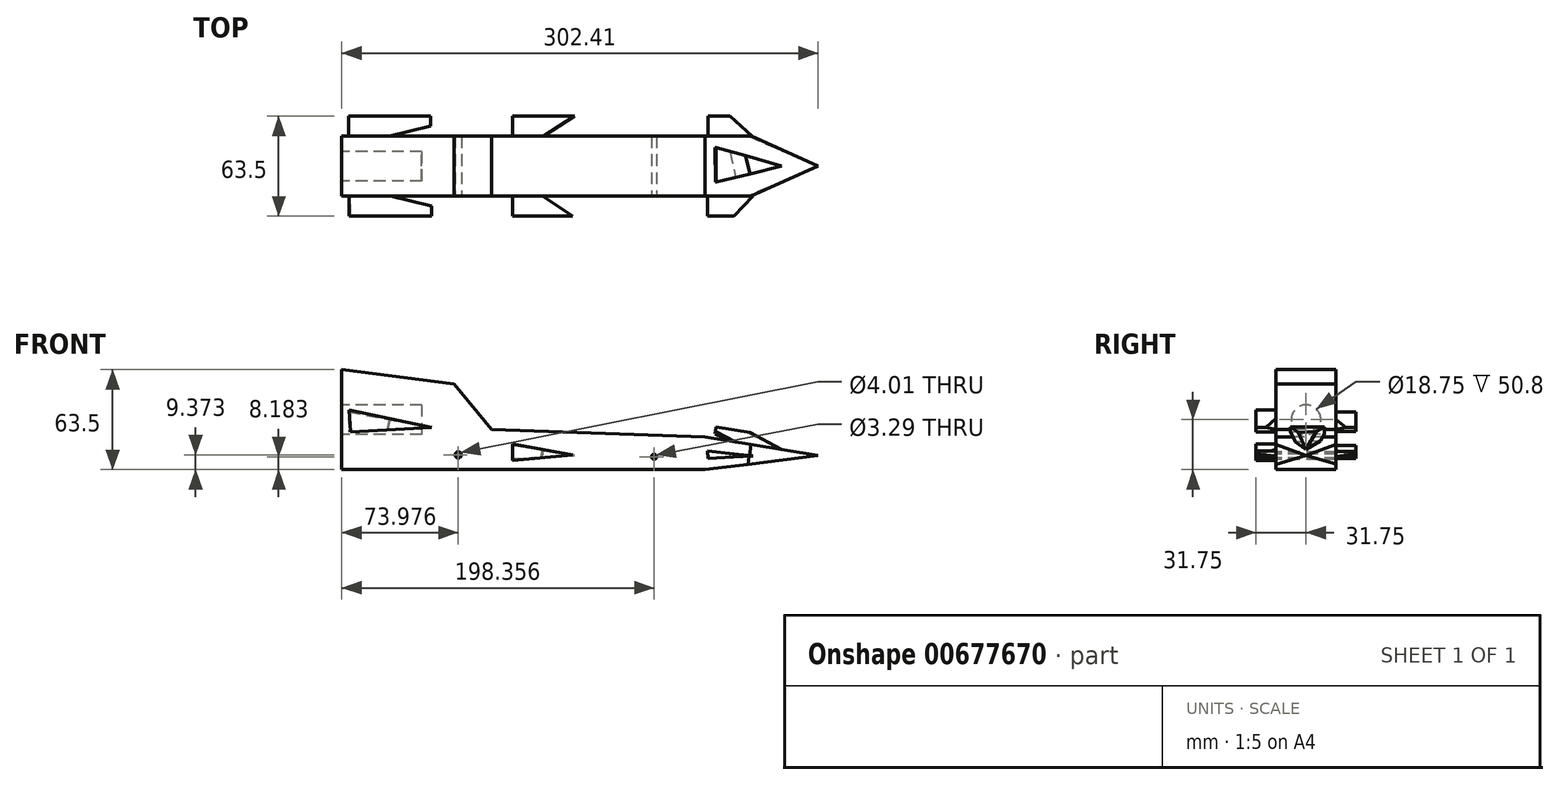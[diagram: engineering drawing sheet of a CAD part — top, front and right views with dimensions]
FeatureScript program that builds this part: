
annotation { "Feature Type Name" : "Feature", "Feature Type Description" : "" }
export const myFeature = defineFeature(function(context is Context, id is Id, definition is map)
    precondition{}
    {
        {
            var Q0;
            Q0=qCreatedBy(makeId("Front.planeOp"),FACE);
            var sketch = newSketch(context, id + "F0", { "sketchPlane" : qUnion([Q0])});
            skLineSegment(sketch, "E0", {"start": v(0, 0) * mm, "end": v(0, 63.5) * mm});
            skLineSegment(sketch, "E1", {"start": v(0, 63.5) * mm, "end": v(302.4, 25.4) * mm});
            skLineSegment(sketch, "E2", {"start": v(302.4, 25.4) * mm, "end": v(302.4, 0) * mm});
            skLineSegment(sketch, "E3", {"start": v(302.4, 0) * mm, "end": v(0, 0) * mm});
            skSolve(sketch);
        }
        {
            var Q0;
            Q0=makeQuery(id+"F0.imprint","IMPRINT",FACE,{"disambiguationData":[TD([[makeQuery(id+"F0.imprint","IMPRINT",EDGE,{"derivedFrom":sQuery(id+"F0.wireOp",EDGE,"E0")}),-1.0]])]});
            extrude(context, id + "F1", {"entities" : qUnion([Q0]), "depth" : 38.1 * mm, "offsetDistance" : 25.4 * mm});
        }
        {
            var Q0;
            Q0=makeQuery(id+"F1.opExtrude","SWEPT_FACE",FACE,{"disambiguationData":[OSD([sQuery(id+"F0.wireOp",EDGE,"E0")])]});
            var sketch = newSketch(context, id + "F2", { "sketchPlane" : qUnion([Q0])});
            skCircle(sketch, "E4", {"center": v(19.05, 31.75) * mm, "radius": 9.38 * mm});
            skPoint(sketch, "E4.centerSnap0", {"position": v(38.1, 31.75) * mm});
            skPoint(sketch, "E4.centerSnap1", {"position": v(19.05, 0) * mm});
            skSolve(sketch);
        }
        {
            var Q0;
            Q0=makeQuery(id+"F1.opExtrude","CAP_FACE",FACE,{"disambiguationData":[OSD([sQuery(id+"F0.wireOp",EDGE,"E0"),sQuery(id+"F0.wireOp",EDGE,"E1"),sQuery(id+"F0.wireOp",EDGE,"E2"),sQuery(id+"F0.wireOp",EDGE,"E3")])],"isStart":false});
            var sketch = newSketch(context, id + "F3", { "sketchPlane" : qUnion([Q0])});
            skLineSegment(sketch, "E5", {"start": v(0, 63.5) * mm, "end": v(71.38, 54.5) * mm});
            skLineSegment(sketch, "E6", {"start": v(71.38, 54.5) * mm, "end": v(95.22, 25.4) * mm});
            skLineSegment(sketch, "E7", {"start": v(95.22, 25.4) * mm, "end": v(302.4, 18.07) * mm});
            skSolve(sketch);
        }
        {
            var Q0;
            {var subQ0=sQuery(id+"F3.wireOp",EDGE,"E6");Q0=makeQuery(id+"F3.imprint","IMPRINT",FACE,{"disambiguationData":[TD([[makeQuery(id+"F3.imprint","IMPRINT",EDGE,{"derivedFrom":subQ0}),1.0]])]});}
            extrude(context, id + "F4", {"entities" : qUnion([Q0]), "operationType" : NewBodyOperationType.REMOVE, "oppositeDirection" : true, "depth" : 38.1 * mm, "offsetDistance" : 25.4 * mm});
        }
        {
            var Q0;
            Q0=makeQuery(id+"F1.opExtrude","CAP_FACE",FACE,{"disambiguationData":[OSD([sQuery(id+"F0.wireOp",EDGE,"E0"),sQuery(id+"F0.wireOp",EDGE,"E1"),sQuery(id+"F0.wireOp",EDGE,"E2"),sQuery(id+"F0.wireOp",EDGE,"E3")])],"isStart":false});
            var sketch = newSketch(context, id + "F5", { "sketchPlane" : qUnion([Q0])});
            skLineSegment(sketch, "E8", {"start": v(302.4, 9.03) * mm, "end": v(230.75, 20.6) * mm});
            skLineSegment(sketch, "E9", {"start": v(302.4, 9.03) * mm, "end": v(232.62, 0) * mm});
            skSolve(sketch);
        }
        {
            var Q0;
            {var subQ0=sQuery(id+"F5.wireOp",EDGE,"E8");Q0=makeQuery(id+"F5.imprint","IMPRINT",FACE,{"disambiguationData":[TD([[makeQuery(id+"F5.imprint","IMPRINT",EDGE,{"derivedFrom":subQ0}),-1.0]])]});}
            extrude(context, id + "F6", {"entities" : qUnion([Q0]), "operationType" : NewBodyOperationType.REMOVE, "oppositeDirection" : true, "depth" : 38.1 * mm, "offsetDistance" : 25.4 * mm});
        }
        {
            var Q0;
            Q0=makeQuery(id+"F1.opExtrude","CAP_FACE",FACE,{"disambiguationData":[OSD([sQuery(id+"F0.wireOp",EDGE,"E0"),sQuery(id+"F0.wireOp",EDGE,"E1"),sQuery(id+"F0.wireOp",EDGE,"E2"),sQuery(id+"F0.wireOp",EDGE,"E3")])],"isStart":false});
            var sketch = newSketch(context, id + "F7", { "sketchPlane" : qUnion([Q0])});
            skLineSegment(sketch, "E10", {"start": v(302.4, 9.03) * mm, "end": v(230.75, 0) * mm});
            skSolve(sketch);
        }
        {
            var Q0;
            {var subQ0=sQuery(id+"F7.wireOp",EDGE,"E10");Q0=makeQuery(id+"F7.imprint","IMPRINT",FACE,{"disambiguationData":[TD([[makeQuery(id+"F7.imprint","IMPRINT",EDGE,{"derivedFrom":subQ0}),1.0]])]});}
            extrude(context, id + "F8", {"entities" : qUnion([Q0]), "operationType" : NewBodyOperationType.REMOVE, "oppositeDirection" : true, "depth" : 38.1 * mm, "offsetDistance" : 25.4 * mm});
        }
        {
            var Q0;
            Q0=qCreatedBy(makeId("Front.planeOp"),FACE);
            var sketch = newSketch(context, id + "F9", { "sketchPlane" : qUnion([Q0])});
            skLineSegment(sketch, "E11", {"start": v(4.35, 36.75) * mm, "end": v(4.35, 24.25) * mm});
            skLineSegment(sketch, "E12", {"start": v(4.35, 24.25) * mm, "end": v(56.42, 26.93) * mm});
            skLineSegment(sketch, "E13", {"start": v(56.42, 26.93) * mm, "end": v(4.35, 36.75) * mm});
            skLineSegment(sketch, "E14", {"start": v(108.5, 15.32) * mm, "end": v(108.92, 7.01) * mm});
            skLineSegment(sketch, "E15", {"start": v(108.92, 7.01) * mm, "end": v(147.83, 9.02) * mm});
            skLineSegment(sketch, "E16", {"start": v(147.83, 9.02) * mm, "end": v(108.5, 15.32) * mm});
            skLineSegment(sketch, "E17", {"start": v(232.28, 11.75) * mm, "end": v(232.52, 7.01) * mm});
            skLineSegment(sketch, "E18", {"start": v(232.52, 7.01) * mm, "end": v(261.1, 8.48) * mm});
            skLineSegment(sketch, "E19", {"start": v(261.1, 8.48) * mm, "end": v(232.28, 11.75) * mm});
            skSolve(sketch);
        }
        {
            var Q0;
            Q0=makeQuery(id+"F1.opExtrude","CAP_FACE",FACE,{"disambiguationData":[OSD([sQuery(id+"F0.wireOp",EDGE,"E0"),sQuery(id+"F0.wireOp",EDGE,"E1"),sQuery(id+"F0.wireOp",EDGE,"E2"),sQuery(id+"F0.wireOp",EDGE,"E3")])],"isStart":false});
            var sketch = newSketch(context, id + "F10", { "sketchPlane" : qUnion([Q0])});
            skLineSegment(sketch, "E20", {"start": v(4.65, 37.94) * mm, "end": v(57.02, 26.9) * mm});
            skLineSegment(sketch, "E21", {"start": v(57.02, 26.9) * mm, "end": v(5.72, 24.04) * mm});
            skLineSegment(sketch, "E22", {"start": v(5.72, 24.04) * mm, "end": v(4.65, 37.94) * mm});
            skSolve(sketch);
        }
        {
            var Q0;
            Q0=makeQuery(id+"F10.imprint","IMPRINT",FACE,{"disambiguationData":[TD([[makeQuery(id+"F10.imprint","IMPRINT",EDGE,{"derivedFrom":sQuery(id+"F10.wireOp",EDGE,"E20")}),-1.0]])]});
            extrude(context, id + "F11", {"entities" : qUnion([Q0]), "operationType" : NewBodyOperationType.ADD, "depth" : 12.7 * mm, "offsetDistance" : 25.4 * mm});
        }
        {
            var Q0;
            Q0=makeQuery(id+"F1.opExtrude","CAP_FACE",FACE,{"disambiguationData":[OSD([sQuery(id+"F0.wireOp",EDGE,"E0"),sQuery(id+"F0.wireOp",EDGE,"E1"),sQuery(id+"F0.wireOp",EDGE,"E2"),sQuery(id+"F0.wireOp",EDGE,"E3")])],"isStart":false});
            var sketch = newSketch(context, id + "F12", { "sketchPlane" : qUnion([Q0])});
            skLineSegment(sketch, "E23", {"start": v(108.5, 16.22) * mm, "end": v(108.5, 5.8) * mm});
            skLineSegment(sketch, "E24", {"start": v(108.5, 5.8) * mm, "end": v(146.58, 9.37) * mm});
            skLineSegment(sketch, "E25", {"start": v(146.58, 9.37) * mm, "end": v(108.5, 16.22) * mm});
            skSolve(sketch);
        }
        {
            var Q0;
            Q0 = qSketchRegion(id + "F12", true);
            extrude(context, id + "F13", {"entities" : qUnion([Q0]), "operationType" : NewBodyOperationType.ADD, "depth" : 12.7 * mm, "offsetDistance" : 25.4 * mm});
        }
        {
            var Q0;
            Q0=makeQuery(id+"F1.opExtrude","CAP_FACE",FACE,{"disambiguationData":[OSD([sQuery(id+"F0.wireOp",EDGE,"E0"),sQuery(id+"F0.wireOp",EDGE,"E1"),sQuery(id+"F0.wireOp",EDGE,"E2"),sQuery(id+"F0.wireOp",EDGE,"E3")])],"isStart":false});
            var sketch = newSketch(context, id + "F14", { "sketchPlane" : qUnion([Q0])});
            skLineSegment(sketch, "E26", {"start": v(232.26, 11.81) * mm, "end": v(232.53, 7.14) * mm});
            skLineSegment(sketch, "E27", {"start": v(232.53, 7.14) * mm, "end": v(261.08, 8.54) * mm});
            skLineSegment(sketch, "E28", {"start": v(261.08, 8.54) * mm, "end": v(232.26, 11.81) * mm});
            skSolve(sketch);
        }
        {
            var Q0;
            Q0=makeQuery(id+"F14.imprint","IMPRINT",FACE,{"disambiguationData":[TD([[makeQuery(id+"F14.imprint","IMPRINT",EDGE,{"derivedFrom":sQuery(id+"F14.wireOp",EDGE,"E26")}),1.0]])]});
            extrude(context, id + "F15", {"entities" : qUnion([Q0]), "operationType" : NewBodyOperationType.ADD, "depth" : 12.7 * mm, "offsetDistance" : 25.4 * mm});
        }
        {
            var Q0;
            Q0=makeQuery(id+"F13.opExtrude","SWEPT_FACE",FACE,{"disambiguationData":[OSD([sQuery(id+"F12.wireOp",EDGE,"E25")])]});
            var sketch = newSketch(context, id + "F16", { "sketchPlane" : qUnion([Q0])});
            skLineSegment(sketch, "E29", {"start": v(142.61, -50.8) * mm, "end": v(123.26, -38.1) * mm});
            skSolve(sketch);
        }
        {
            var Q0;
            {var subQ0=sQuery(id+"F16.wireOp",EDGE,"E29");Q0=makeQuery(id+"F16.imprint","IMPRINT",FACE,{"disambiguationData":[TD([[makeQuery(id+"F16.imprint","IMPRINT",EDGE,{"derivedFrom":subQ0}),-1.0]])]});}
            extrude(context, id + "F17", {"entities" : qUnion([Q0]), "operationType" : NewBodyOperationType.REMOVE, "oppositeDirection" : true, "depth" : 25.4 * mm, "offsetDistance" : 25.4 * mm});
        }
        {
            var Q0;
            Q0=makeQuery(id+"F6.boolean.opBoolean","COPY",FACE,{"derivedFrom":makeQuery(id+"F6.opExtrude","SWEPT_FACE",FACE,{"disambiguationData":[OSD([sQuery(id+"F5.wireOp",EDGE,"E8")])]})});
            var sketch = newSketch(context, id + "F18", { "sketchPlane" : qUnion([Q0])});
            skLineSegment(sketch, "E30", {"start": v(230.38, -7.3) * mm, "end": v(230.38, -29.03) * mm});
            skLineSegment(sketch, "E31", {"start": v(273.67, -19.05) * mm, "end": v(230.38, -7.3) * mm});
            skPoint(sketch, "E31.startSnap0", {"position": v(224.52, -19.05) * mm});
            skLineSegment(sketch, "E32", {"start": v(273.67, -19.05) * mm, "end": v(230.38, -29.03) * mm});
            skSolve(sketch);
        }
        {
            var Q0;
            Q0=makeQuery(id+"F18.imprint","IMPRINT",FACE,{"disambiguationData":[TD([[makeQuery(id+"F18.imprint","IMPRINT",EDGE,{"derivedFrom":sQuery(id+"F18.wireOp",EDGE,"E30")}),1.0]])]});
            extrude(context, id + "F19", {"entities" : qUnion([Q0]), "operationType" : NewBodyOperationType.ADD, "depth" : 7.62 * mm, "offsetDistance" : 25.4 * mm});
        }
        {
            var Q0;
            Q0=makeQuery(id+"F19.opExtrude","SWEPT_FACE",FACE,{"disambiguationData":[OSD([sQuery(id+"F18.wireOp",EDGE,"E32")])]});
            var sketch = newSketch(context, id + "F20", { "sketchPlane" : qUnion([Q0])});
            skLineSegment(sketch, "E33", {"start": v(225.1, 25.17) * mm, "end": v(238.26, 18.42) * mm});
            skSolve(sketch);
        }
        {
            var Q0;
            {var subQ0=sQuery(id+"F20.wireOp",EDGE,"E33");Q0=makeQuery(id+"F20.imprint","IMPRINT",FACE,{"disambiguationData":[TD([[makeQuery(id+"F20.imprint","IMPRINT",EDGE,{"derivedFrom":subQ0}),-1.0]])]});}
            extrude(context, id + "F21", {"entities" : qUnion([Q0]), "operationType" : NewBodyOperationType.REMOVE, "oppositeDirection" : true, "depth" : 25.4 * mm, "offsetDistance" : 25.4 * mm});
        }
        {
            var Q0;
            Q0=makeQuery(id+"F9.imprint","IMPRINT",FACE,{"disambiguationData":[TD([[makeQuery(id+"F9.imprint","IMPRINT",EDGE,{"derivedFrom":sQuery(id+"F9.wireOp",EDGE,"E11")}),1.0]])]});
            var sketch = newSketch(context, id + "F22", { "sketchPlane" : qUnion([Q0])});
            skLineSegment(sketch, "E34", {"start": v(4.03, 23.93) * mm, "end": v(4.03, 36.61) * mm});
            skLineSegment(sketch, "E35", {"start": v(4.03, 36.61) * mm, "end": v(56.41, 26.92) * mm});
            skLineSegment(sketch, "E36", {"start": v(56.41, 26.92) * mm, "end": v(4.03, 23.93) * mm});
            skSolve(sketch);
        }
        {
            var Q0;
            {var subQ0=sQuery(id+"F22.wireOp",EDGE,"E35");var subQ1=makeQuery(id+"F9.imprint","IMPRINT",EDGE,{"derivedFrom":sQuery(id+"F9.wireOp",EDGE,"E11")});var subQ2=makeQuery(id+"F22.imprint","INTERSECT",VERTEX,{"derivedFrom":[subQ1,subQ0]});Q0=makeQuery(id+"F22.imprint","IMPRINT",FACE,{"disambiguationData":[TD([[makeQuery(id+"F22.imprint","IMPRINT",EDGE,{"disambiguationData":[TD([[subQ2,-1.0]])],"derivedFrom":subQ0}),-1.0]])]});}
            extrude(context, id + "F23", {"entities" : qUnion([Q0]), "operationType" : NewBodyOperationType.ADD, "oppositeDirection" : true, "depth" : 12.7 * mm, "offsetDistance" : 25.4 * mm});
        }
        {
            var Q0;
            Q0=makeQuery(id+"F9.imprint","IMPRINT",FACE,{"disambiguationData":[TD([[makeQuery(id+"F9.imprint","IMPRINT",EDGE,{"derivedFrom":sQuery(id+"F9.wireOp",EDGE,"E17")}),1.0]])]});
            var sketch = newSketch(context, id + "F24", { "sketchPlane" : qUnion([Q0])});
            skLineSegment(sketch, "E37", {"start": v(232.46, 6.36) * mm, "end": v(232.46, 11.64) * mm});
            skLineSegment(sketch, "E38", {"start": v(232.46, 11.64) * mm, "end": v(261.11, 8.4) * mm});
            skLineSegment(sketch, "E39", {"start": v(261.11, 8.4) * mm, "end": v(232.46, 6.36) * mm});
            skSolve(sketch);
        }
        {
            var Q0;
            {var subQ0=sQuery(id+"F24.wireOp",EDGE,"E38");var subQ1=sQuery(id+"F24.wireOp",EDGE,"E37");var subQ2=makeQuery(id+"F24.imprint","INTERSECT",VERTEX,{"derivedFrom":[subQ1,subQ0]});Q0=makeQuery(id+"F24.imprint","IMPRINT",FACE,{"disambiguationData":[TD([[makeQuery(id+"F24.imprint","IMPRINT",EDGE,{"disambiguationData":[TD([[subQ2,1.0]])],"derivedFrom":subQ1}),-1.0]])]});}
            extrude(context, id + "F25", {"entities" : qUnion([Q0]), "operationType" : NewBodyOperationType.ADD, "oppositeDirection" : true, "depth" : 12.7 * mm, "offsetDistance" : 25.4 * mm});
        }
        {
            var Q0;
            Q0=makeQuery(id+"F9.imprint","IMPRINT",FACE,{"disambiguationData":[TD([[makeQuery(id+"F9.imprint","IMPRINT",EDGE,{"derivedFrom":sQuery(id+"F9.wireOp",EDGE,"E14")}),1.0]])]});
            extrude(context, id + "F26", {"entities" : qUnion([Q0]), "operationType" : NewBodyOperationType.ADD, "oppositeDirection" : true, "depth" : 12.7 * mm, "offsetDistance" : 25.4 * mm});
        }
        {
            var Q0;
            Q0=makeQuery(id+"F26.opExtrude","SWEPT_FACE",FACE,{"disambiguationData":[OSD([sQuery(id+"F9.wireOp",EDGE,"E16")])]});
            var sketch = newSketch(context, id + "F27", { "sketchPlane" : qUnion([Q0])});
            skLineSegment(sketch, "E40", {"start": v(124.62, 0) * mm, "end": v(144.54, 12.7) * mm});
            skSolve(sketch);
        }
        {
            var Q0;
            {var subQ0=sQuery(id+"F27.wireOp",EDGE,"E40");Q0=makeQuery(id+"F27.imprint","IMPRINT",FACE,{"disambiguationData":[TD([[makeQuery(id+"F27.imprint","IMPRINT",EDGE,{"derivedFrom":subQ0}),-1.0]])]});}
            extrude(context, id + "F28", {"entities" : qUnion([Q0]), "operationType" : NewBodyOperationType.REMOVE, "oppositeDirection" : true, "depth" : 25.4 * mm, "offsetDistance" : 25.4 * mm});
        }
        {
            var Q0;
            Q0=makeQuery(id+"F25.opExtrude","SWEPT_FACE",FACE,{"disambiguationData":[OSD([sQuery(id+"F24.wireOp",EDGE,"E38")])]});
            var sketch = newSketch(context, id + "F29", { "sketchPlane" : qUnion([Q0])});
            skLineSegment(sketch, "E41", {"start": v(243.8, 12.7) * mm, "end": v(257.94, 0) * mm});
            skSolve(sketch);
        }
        {
            var Q0;
            {var subQ0=sQuery(id+"F29.wireOp",EDGE,"E41");Q0=makeQuery(id+"F29.imprint","IMPRINT",FACE,{"disambiguationData":[TD([[makeQuery(id+"F29.imprint","IMPRINT",EDGE,{"derivedFrom":subQ0}),1.0]])]});}
            extrude(context, id + "F30", {"entities" : qUnion([Q0]), "operationType" : NewBodyOperationType.REMOVE, "oppositeDirection" : true, "depth" : 25.4 * mm, "offsetDistance" : 25.4 * mm});
        }
        {
            var Q0;
            Q0=makeQuery(id+"F15.opExtrude","SWEPT_FACE",FACE,{"disambiguationData":[OSD([sQuery(id+"F14.wireOp",EDGE,"E28")])]});
            var sketch = newSketch(context, id + "F31", { "sketchPlane" : qUnion([Q0])});
            skLineSegment(sketch, "E42", {"start": v(258.45, -38.1) * mm, "end": v(246.23, -50.8) * mm});
            skSolve(sketch);
        }
        {
            var Q0;
            {var subQ0=sQuery(id+"F31.wireOp",EDGE,"E42");Q0=makeQuery(id+"F31.imprint","IMPRINT",FACE,{"disambiguationData":[TD([[makeQuery(id+"F31.imprint","IMPRINT",EDGE,{"derivedFrom":subQ0}),1.0]])]});}
            extrude(context, id + "F32", {"entities" : qUnion([Q0]), "operationType" : NewBodyOperationType.REMOVE, "oppositeDirection" : true, "depth" : 25.4 * mm, "offsetDistance" : 25.4 * mm});
        }
        {
            var Q0;
            Q0=makeQuery(id+"F19.opExtrude","SWEPT_FACE",FACE,{"disambiguationData":[OSD([sQuery(id+"F18.wireOp",EDGE,"E32")])]});
            var sketch = newSketch(context, id + "F33", { "sketchPlane" : qUnion([Q0])});
            skLineSegment(sketch, "E43", {"start": v(247.54, 24.6) * mm, "end": v(268.2, 13.46) * mm});
            skLineSegment(sketch, "E44", {"start": v(269.45, 20.98) * mm, "end": v(247.54, 24.6) * mm});
            skSolve(sketch);
        }
        {
            var Q0;
            Q0=makeQuery(id+"F33.imprint","IMPRINT",FACE,{"disambiguationData":[TD([[makeQuery(id+"F33.imprint","IMPRINT",EDGE,{"derivedFrom":sQuery(id+"F33.wireOp",EDGE,"E43")}),1.0]])]});
            extrude(context, id + "F34", {"entities" : qUnion([Q0]), "operationType" : NewBodyOperationType.REMOVE, "oppositeDirection" : true, "depth" : 25.4 * mm, "offsetDistance" : 25.4 * mm});
        }
        {
            var Q0;
            Q0=makeQuery(id+"F11.opExtrude","SWEPT_FACE",FACE,{"disambiguationData":[OSD([sQuery(id+"F10.wireOp",EDGE,"E20")])]});
            var sketch = newSketch(context, id + "F35", { "sketchPlane" : qUnion([Q0])});
            skLineSegment(sketch, "E45", {"start": v(50.25, -50.8) * mm, "end": v(50.25, -44.45) * mm});
            skLineSegment(sketch, "E46", {"start": v(50.25, -44.45) * mm, "end": v(23.49, -38.1) * mm});
            skSolve(sketch);
        }
        {
            var Q0;
            {var subQ0=sQuery(id+"F35.wireOp",EDGE,"E46");Q0=makeQuery(id+"F35.imprint","IMPRINT",FACE,{"disambiguationData":[TD([[makeQuery(id+"F35.imprint","IMPRINT",EDGE,{"derivedFrom":subQ0}),-1.0]])]});}
            extrude(context, id + "F36", {"entities" : qUnion([Q0]), "operationType" : NewBodyOperationType.REMOVE, "oppositeDirection" : true, "depth" : 25.4 * mm, "offsetDistance" : 25.4 * mm});
        }
        {
            var Q0;
            Q0=makeQuery(id+"F23.opExtrude","SWEPT_FACE",FACE,{"disambiguationData":[OSD([sQuery(id+"F22.wireOp",EDGE,"E35")])]});
            var sketch = newSketch(context, id + "F37", { "sketchPlane" : qUnion([Q0])});
            skLineSegment(sketch, "E47", {"start": v(50.55, 12.7) * mm, "end": v(50.55, 6.35) * mm});
            skLineSegment(sketch, "E48", {"start": v(50.55, 6.35) * mm, "end": v(24.09, 0) * mm});
            skSolve(sketch);
        }
        {
            var Q0;
            {var subQ0=sQuery(id+"F37.wireOp",EDGE,"E48");Q0=makeQuery(id+"F37.imprint","IMPRINT",FACE,{"disambiguationData":[TD([[makeQuery(id+"F37.imprint","IMPRINT",EDGE,{"derivedFrom":subQ0}),1.0]])]});}
            extrude(context, id + "F38", {"entities" : qUnion([Q0]), "operationType" : NewBodyOperationType.REMOVE, "oppositeDirection" : true, "depth" : 25.4 * mm, "offsetDistance" : 25.4 * mm});
        }
        {
            var Q0;
            Q0=makeQuery(id+"F2.imprint","IMPRINT",FACE,{"disambiguationData":[TD([[makeQuery(id+"F2.imprint","IMPRINT",EDGE,{"derivedFrom":sQuery(id+"F2.wireOp",EDGE,"E4")}),1.0]])]});
            extrude(context, id + "F39", {"entities" : qUnion([Q0]), "operationType" : NewBodyOperationType.REMOVE, "oppositeDirection" : true, "depth" : 50.8 * mm, "offsetDistance" : 25.4 * mm});
        }
        {
            var Q0;
            Q0=makeQuery(id+"F21.boolean.opBoolean","MERGE",FACE,{"derivedFrom":[makeQuery(id+"F6.boolean.opBoolean","COPY",FACE,{"derivedFrom":makeQuery(id+"F6.opExtrude","SWEPT_FACE",FACE,{"disambiguationData":[OSD([sQuery(id+"F5.wireOp",EDGE,"E8")])]})}),makeQuery(id+"F21.opExtrude","SWEPT_FACE",FACE,{"disambiguationData":[OSD([sQuery(id+"F18.wireOp",EDGE,"E32")])]})]});
            var sketch = newSketch(context, id + "F40", { "sketchPlane" : qUnion([Q0])});
            skLineSegment(sketch, "E49", {"start": v(254.4, 0) * mm, "end": v(297.1, -19.05) * mm});
            skLineSegment(sketch, "E50", {"start": v(297.1, -19.05) * mm, "end": v(255.3, -38.1) * mm});
            skSolve(sketch);
        }
        {
            var Q0;
            {var subQ0=sQuery(id+"F40.wireOp",EDGE,"E49");Q0=makeQuery(id+"F40.imprint","IMPRINT",FACE,{"disambiguationData":[TD([[makeQuery(id+"F40.imprint","IMPRINT",EDGE,{"derivedFrom":subQ0}),1.0]])]});}
            extrude(context, id + "F41", {"entities" : qUnion([Q0]), "operationType" : NewBodyOperationType.REMOVE, "oppositeDirection" : true, "depth" : 25.4 * mm, "offsetDistance" : 25.4 * mm});
        }
        {
            var Q0;
            Q0=makeQuery(id+"F21.boolean.opBoolean","MERGE",FACE,{"derivedFrom":[makeQuery(id+"F6.boolean.opBoolean","COPY",FACE,{"derivedFrom":makeQuery(id+"F6.opExtrude","SWEPT_FACE",FACE,{"disambiguationData":[OSD([sQuery(id+"F5.wireOp",EDGE,"E8")])]})}),makeQuery(id+"F21.opExtrude","SWEPT_FACE",FACE,{"disambiguationData":[OSD([sQuery(id+"F18.wireOp",EDGE,"E32")])]})]});
            var sketch = newSketch(context, id + "F42", { "sketchPlane" : qUnion([Q0])});
            skLineSegment(sketch, "E51", {"start": v(297.1, -19.05) * mm, "end": v(254.1, -38.1) * mm});
            skSolve(sketch);
        }
        {
            var Q0;
            {var subQ0=sQuery(id+"F42.wireOp",EDGE,"E51");Q0=makeQuery(id+"F42.imprint","IMPRINT",FACE,{"disambiguationData":[TD([[makeQuery(id+"F42.imprint","IMPRINT",EDGE,{"derivedFrom":subQ0}),1.0]])]});}
            extrude(context, id + "F43", {"entities" : qUnion([Q0]), "operationType" : NewBodyOperationType.REMOVE, "oppositeDirection" : true, "depth" : 25.4 * mm, "offsetDistance" : 25.4 * mm});
        }
        {
            var Q0;
            Q0=makeQuery(id+"F36.boolean.opBoolean","MERGE",FACE,{"derivedFrom":[makeQuery(id+"F17.boolean.opBoolean","MERGE",FACE,{"derivedFrom":[makeQuery(id+"F1.opExtrude","CAP_FACE",FACE,{"disambiguationData":[OSD([sQuery(id+"F0.wireOp",EDGE,"E0"),sQuery(id+"F0.wireOp",EDGE,"E1"),sQuery(id+"F0.wireOp",EDGE,"E2"),sQuery(id+"F0.wireOp",EDGE,"E3")])],"isStart":false}),makeQuery(id+"F17.opExtrude","SWEPT_FACE",FACE,{"disambiguationData":[OSD([sQuery(id+"F12.wireOp",EDGE,"E25")])]})]}),makeQuery(id+"F36.opExtrude","SWEPT_FACE",FACE,{"disambiguationData":[OSD([sQuery(id+"F10.wireOp",EDGE,"E20")])]})]});
            var sketch = newSketch(context, id + "F44", { "sketchPlane" : qUnion([Q0])});
            skCircle(sketch, "E52", {"center": v(198.36, 8.18) * mm, "radius": 1.64 * mm});
            skCircle(sketch, "E53", {"center": v(73.98, 9.37) * mm, "radius": 2 * mm});
            skSolve(sketch);
        }
        {
            var Q0;
            Q0=makeQuery(id+"F44.imprint","IMPRINT",FACE,{"disambiguationData":[TD([[makeQuery(id+"F44.imprint","IMPRINT",EDGE,{"derivedFrom":sQuery(id+"F44.wireOp",EDGE,"E52")}),1.0]])]});
            var Q1;
            Q1=makeQuery(id+"F44.imprint","IMPRINT",FACE,{"disambiguationData":[TD([[makeQuery(id+"F44.imprint","IMPRINT",EDGE,{"derivedFrom":sQuery(id+"F44.wireOp",EDGE,"E53")}),1.0]])]});
            extrude(context, id + "F45", {"entities" : qUnion([Q0, Q1]), "operationType" : NewBodyOperationType.REMOVE, "oppositeDirection" : true, "depth" : 50.8 * mm, "offsetDistance" : 25.4 * mm});
        }
    });
